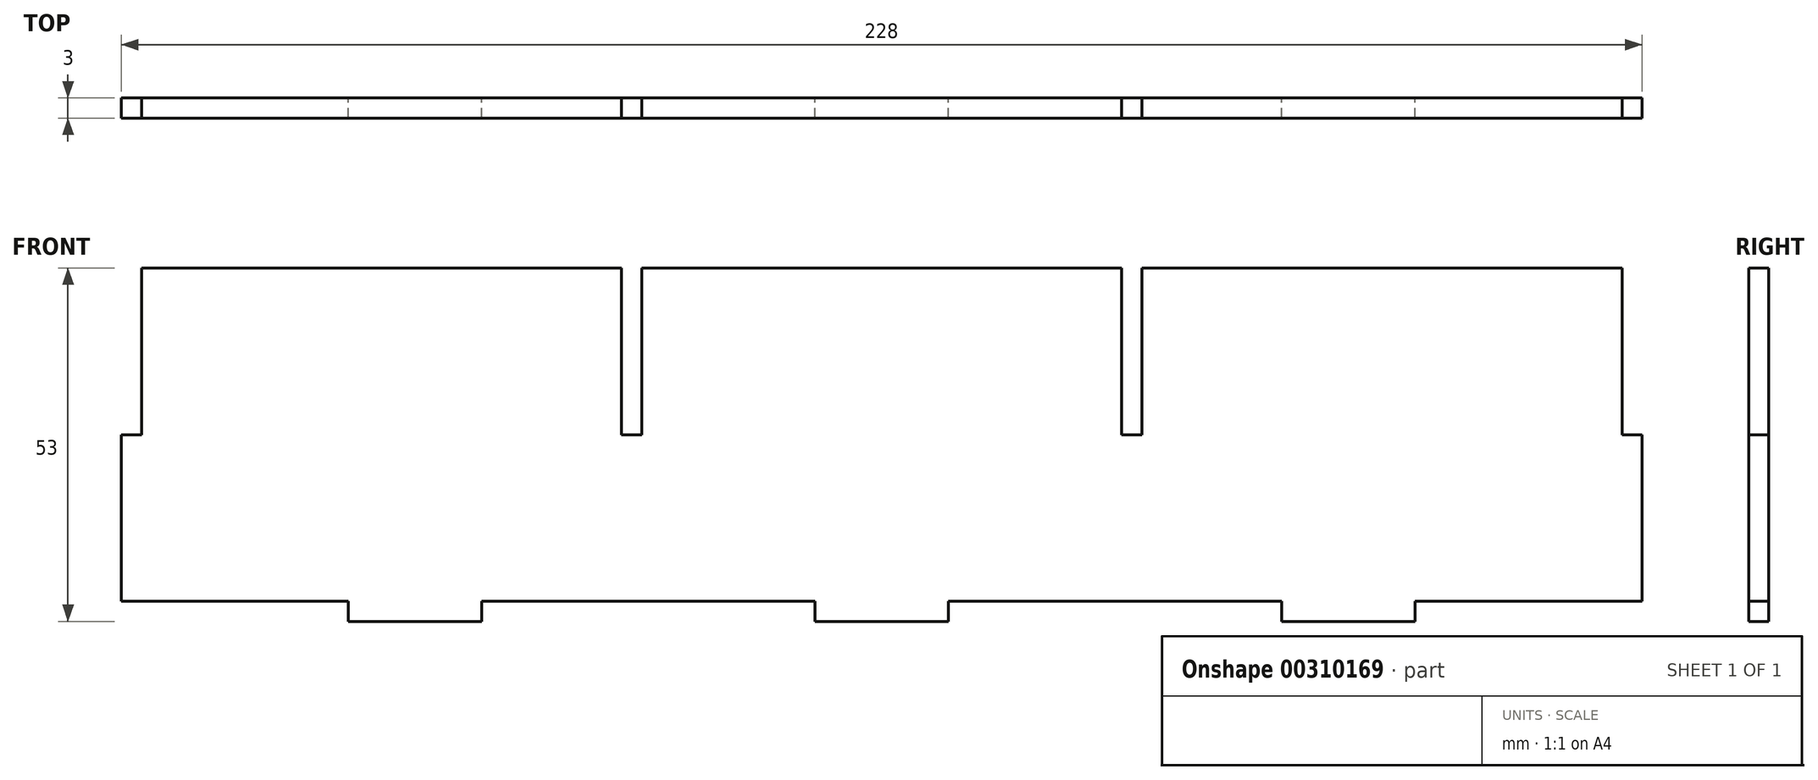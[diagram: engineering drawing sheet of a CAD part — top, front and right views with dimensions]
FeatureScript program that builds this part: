
annotation { "Feature Type Name" : "Feature", "Feature Type Description" : "" }
export const myFeature = defineFeature(function(context is Context, id is Id, definition is map)
    precondition{}
    {
        {
            var Q0;
            Q0=qCreatedBy(makeId("Front.planeOp"),FACE);
            var sketch = newSketch(context, id + "F0", { "sketchPlane" : qUnion([Q0])});
            skLineSegment(sketch, "E0.bottom", {"start": v(114, -25) * mm, "end": v(80, -25) * mm});
            skLineSegment(sketch, "E0.top", {"start": v(114, 25) * mm, "end": v(39, 25) * mm});
            skLineSegment(sketch, "E0.left", {"start": v(114, -25) * mm, "end": v(114, 25) * mm});
            skLineSegment(sketch, "E0.right", {"start": v(-114, -25) * mm, "end": v(-114, 25) * mm});
            skPoint(sketch, "E0.middle", {"position": v(0, 0) * mm});
            skLineSegment(sketch, "E1.top", {"start": v(-80, -28) * mm, "end": v(-60, -28) * mm});
            skLineSegment(sketch, "E1.left", {"start": v(-80, -25) * mm, "end": v(-80, -28) * mm});
            skLineSegment(sketch, "E1.right", {"start": v(-60, -25) * mm, "end": v(-60, -28) * mm});
            skLineSegment(sketch, "E2.top", {"start": v(-10, -28) * mm, "end": v(10, -28) * mm});
            skLineSegment(sketch, "E2.left", {"start": v(-10, -25) * mm, "end": v(-10, -28) * mm});
            skLineSegment(sketch, "E2.right", {"start": v(10, -25) * mm, "end": v(10, -28) * mm});
            skLineSegment(sketch, "E3.top", {"start": v(60, -28) * mm, "end": v(80, -28) * mm});
            skLineSegment(sketch, "E3.left", {"start": v(60, -25) * mm, "end": v(60, -28) * mm});
            skLineSegment(sketch, "E3.right", {"start": v(80, -25) * mm, "end": v(80, -28) * mm});
            skLineSegment(sketch, "E4.trimOffspring", {"start": v(-80, -25) * mm, "end": v(-114, -25) * mm});
            skLineSegment(sketch, "E5.trimOffspring", {"start": v(60, -25) * mm, "end": v(10, -25) * mm});
            skLineSegment(sketch, "E6.trimOffspring", {"start": v(-10, -25) * mm, "end": v(-60, -25) * mm});
            skLineSegment(sketch, "E7.bottom", {"start": v(-114, 25) * mm, "end": v(-111, 25) * mm});
            skLineSegment(sketch, "E7.top", {"start": v(-114, 0) * mm, "end": v(-111, 0) * mm});
            skLineSegment(sketch, "E7.left", {"start": v(-114, 25) * mm, "end": v(-114, 0) * mm});
            skLineSegment(sketch, "E7.right", {"start": v(-111, 25) * mm, "end": v(-111, 0) * mm});
            skLineSegment(sketch, "E8.bottom", {"start": v(114, 25) * mm, "end": v(111, 25) * mm});
            skLineSegment(sketch, "E8.top", {"start": v(114, 0) * mm, "end": v(111, 0) * mm});
            skLineSegment(sketch, "E8.left", {"start": v(114, 25) * mm, "end": v(114, 0) * mm});
            skLineSegment(sketch, "E8.right", {"start": v(111, 25) * mm, "end": v(111, 0) * mm});
            skLineSegment(sketch, "E9.top", {"start": v(-36, 0) * mm, "end": v(-39, 0) * mm});
            skLineSegment(sketch, "E9.left", {"start": v(-36, 25) * mm, "end": v(-36, 0) * mm});
            skLineSegment(sketch, "E9.right", {"start": v(-39, 25) * mm, "end": v(-39, 0) * mm});
            skLineSegment(sketch, "E10.trimOffspring", {"start": v(-39, 25) * mm, "end": v(-114, 25) * mm});
            skLineSegment(sketch, "E11.MirrorCS", {"start": v(36, 0) * mm, "end": v(39, 0) * mm});
            skLineSegment(sketch, "E12.MirrorCS", {"start": v(36, 25) * mm, "end": v(36, 0) * mm});
            skLineSegment(sketch, "E13.MirrorCS", {"start": v(39, 25) * mm, "end": v(39, 0) * mm});
            skLineSegment(sketch, "E14.trimOffspring", {"start": v(36, 25) * mm, "end": v(-36, 25) * mm});
            skSolve(sketch);
        }
        {
            var Q0;
            Q0=makeQuery(id+"F0.imprint","IMPRINT",FACE,{"disambiguationData":[TD([[makeQuery(id+"F0.imprint","IMPRINT",EDGE,{"derivedFrom":sQuery(id+"F0.wireOp",EDGE,"E0.bottom")}),-1.0]])]});
            extrude(context, id + "F1", {"entities" : qUnion([Q0]), "depth" : 3 * mm});
        }
    });
